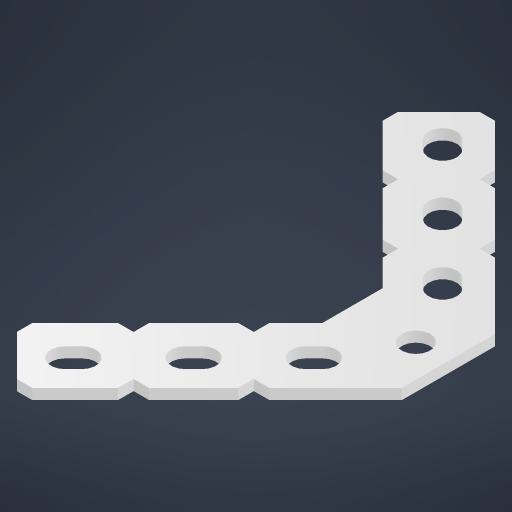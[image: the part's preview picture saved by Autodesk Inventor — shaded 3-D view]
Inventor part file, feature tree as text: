
AUTODESK INVENTOR PART (.ipt)
format: ipt  version: 2024 (Build 280153000, 153)  size: 264,704 bytes
history: native  units: in
note: dims shown in document units (in); Inventor stores cm internally (conversion verified against a paired STEP export)
features: chamfer x1, other x1, imported_body x1
ambient origin geometry x8: Origin, YZ Plane, XZ Plane, XY Plane, X Axis, Y Axis, Z Axis, Center Point
bodies: Body1 (feature_tree)
feature tree (3):
  chamfer  "Chamfer1"  [1 undecoded]
  other  "90-Degree Gusset Plate"
  imported_body  "Base1"
note: 1 required parameter value undecoded (feature->parameter linkage not recoverable at this tier; creation-order binding heuristic only, values carry confidence <= 0.55)
